AUTODESK INVENTOR PART (.ipt)
format: ipt  version: 2020.2 (Build 242310000, 310)  size: 206,336 bytes
history: native  units: mm
features: other x15, sketch x8, revolve x4, extrude x3, fillet x3
ambient origin geometry x8: Origin, YZ Plane, XZ Plane, XY Plane, X Axis, Y Axis, Z Axis, Center Point
bodies: Body1 (feature_tree)
feature tree (33):
  other  "UCS1"
  extrude  "Estrusione2"  Depth=3.0mm
  extrude  "Estrusione3"  TaperAngle=90.0deg  [1 undecoded]
  extrude  "Estrusione4"  Depth=10.0mm
  revolve  "Rivoluzione3"
  revolve  "Rivoluzione4"
  revolve  "Rivoluzione5"
  revolve  "Rivoluzione6"
  fillet  "Raccordo1"  Radius=80.0mm
  fillet  "Raccordo2"  Radius=10.0mm
  fillet  "Raccordo3"  Radius=80.0mm
  other  "PianoY"
  other  "PianoX"
  other  "PianoZ"
  sketch  "Schizzo1"
  sketch  "Schizzo3"
  sketch  "Schizzo4"
  sketch  "Schizzo5"
  sketch  "Schizzo6"
  sketch  "Schizzo7"
  other  "Linea chiusa proiettata1"
  other  "Linea chiusa proiettata2"
  sketch  "Schizzo8"
  other  "Linea chiusa proiettata3"
  sketch  "Schizzo9"
  other  "Linea chiusa proiettata4"
  other  "UCS1: Piano YZ"
  other  "UCS1: Piano XZ"
  other  "UCS1: Piano XY"
  other  "UCS1: Asse X"
  other  "UCS1: Asse Y"
  other  "UCS1: Asse Z"
  other  "UCS1: Punto centrale"
note: 1 required parameter value undecoded (feature->parameter linkage not recoverable at this tier; creation-order binding heuristic only, values carry confidence <= 0.55)
